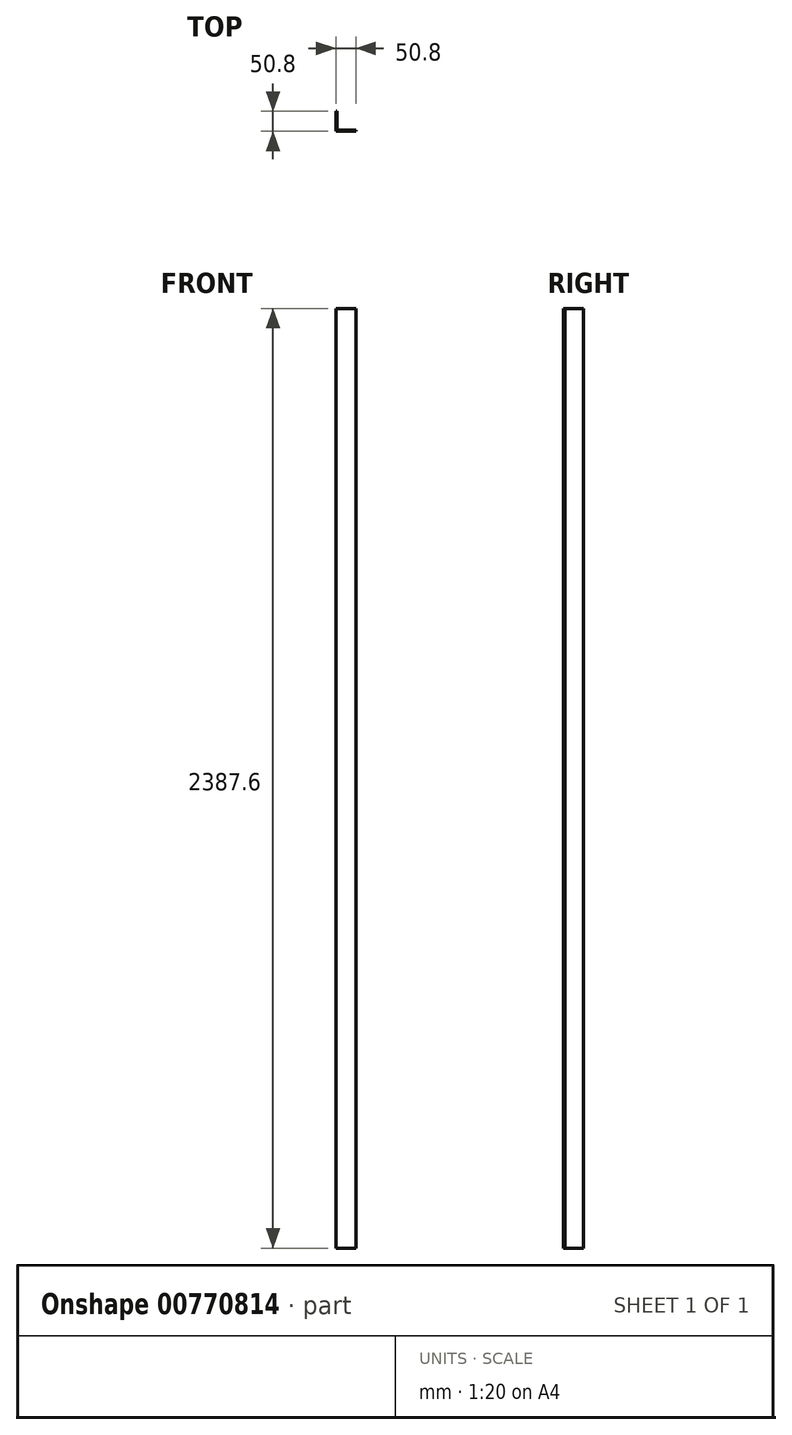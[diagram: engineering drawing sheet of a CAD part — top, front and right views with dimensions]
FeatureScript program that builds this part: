
annotation { "Feature Type Name" : "Feature", "Feature Type Description" : "" }
export const myFeature = defineFeature(function(context is Context, id is Id, definition is map)
    precondition{}
    {
        {
            var Q0;
            Q0=qCreatedBy(makeId("Top.planeOp"),FACE);
            var sketch = newSketch(context, id + "F0", { "sketchPlane" : qUnion([Q0])});
            skLineSegment(sketch, "E0", {"start": v(0, 0) * mm, "end": v(0, 50.8) * mm});
            skLineSegment(sketch, "E1", {"start": v(0, 50.8) * mm, "end": v(3.18, 50.8) * mm});
            skLineSegment(sketch, "E2", {"start": v(3.18, 50.8) * mm, "end": v(3.18, 3.17) * mm});
            skLineSegment(sketch, "E3", {"start": v(3.18, 3.17) * mm, "end": v(50.8, 3.18) * mm});
            skLineSegment(sketch, "E4", {"start": v(50.8, 3.18) * mm, "end": v(50.8, 0) * mm});
            skLineSegment(sketch, "E5", {"start": v(50.8, 0) * mm, "end": v(0, 0) * mm});
            skSolve(sketch);
        }
        {
            var Q0;
            Q0=makeQuery(id+"F0.imprint","IMPRINT",FACE,{"disambiguationData":[TD([[makeQuery(id+"F0.imprint","IMPRINT",EDGE,{"derivedFrom":sQuery(id+"F0.wireOp",EDGE,"E0")}),-1.0]])]});
            extrude(context, id + "F1", {"entities" : qUnion([Q0]), "oppositeDirection" : true, "depth" : 2387.6 * mm, "offsetDistance" : 25.4 * mm});
        }
    });
